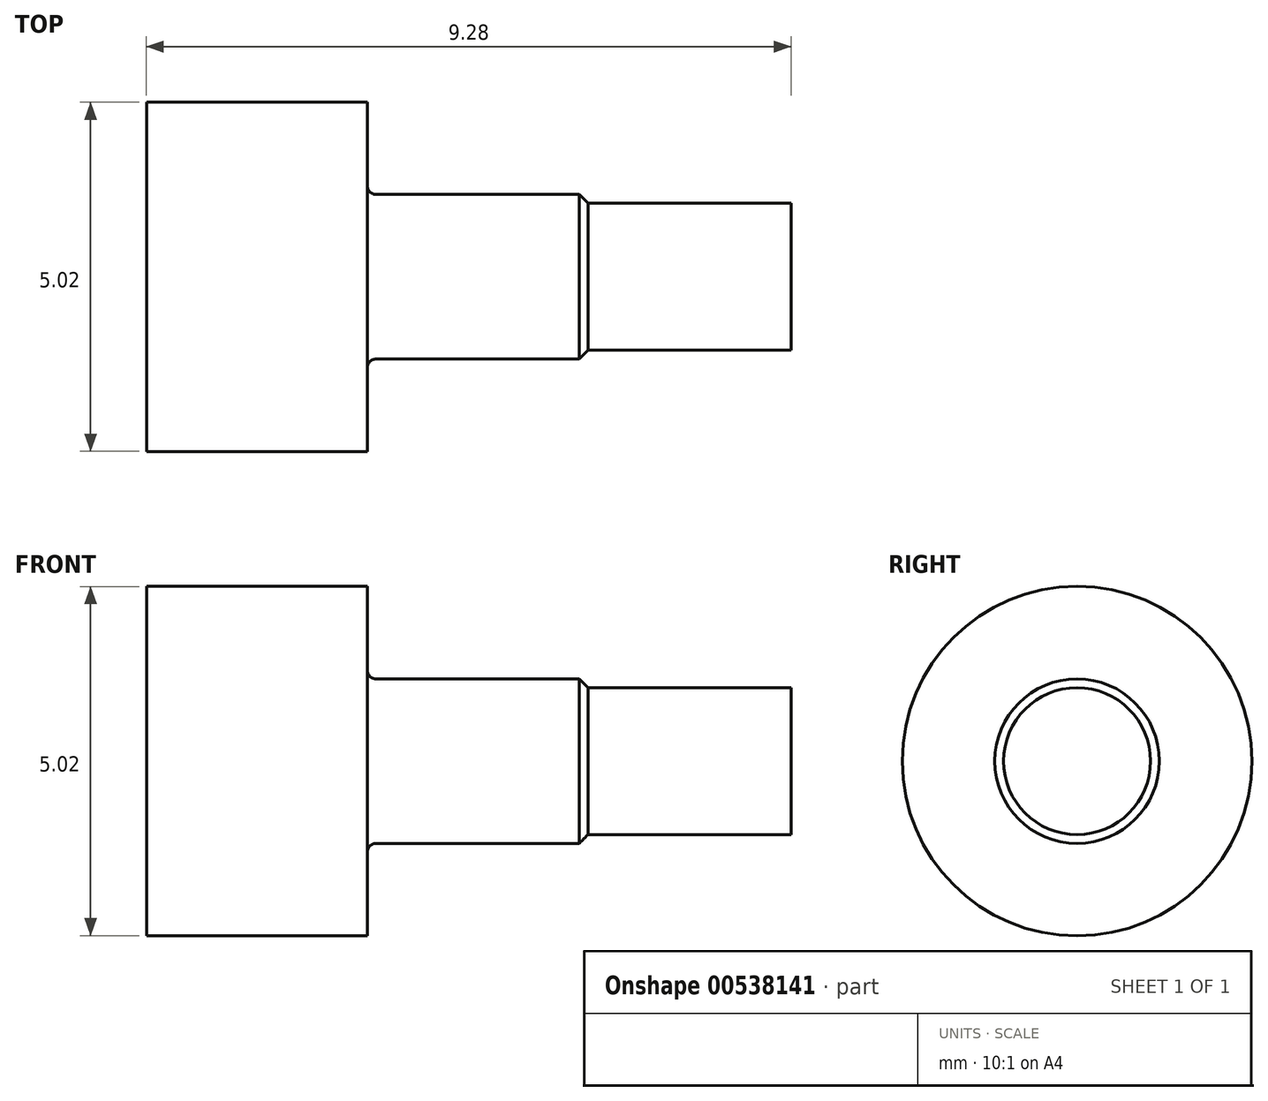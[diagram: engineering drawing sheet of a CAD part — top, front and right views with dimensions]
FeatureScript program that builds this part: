
annotation { "Feature Type Name" : "Feature", "Feature Type Description" : "" }
export const myFeature = defineFeature(function(context is Context, id is Id, definition is map)
    precondition{}
    {
        {
            var Q0;
            Q0=qCreatedBy(makeId("Front.planeOp"),FACE);
            var sketch = newSketch(context, id + "F0", { "sketchPlane" : qUnion([Q0])});
            skLineSegment(sketch, "E0.bottom", {"start": v(0, 0) * mm, "end": v(-3.17, 0) * mm});
            skLineSegment(sketch, "E0.top", {"start": v(0, 2.51) * mm, "end": v(-3.17, 2.51) * mm});
            skLineSegment(sketch, "E0.left", {"start": v(0, 0) * mm, "end": v(0, 2.51) * mm});
            skLineSegment(sketch, "E0.right", {"start": v(-3.18, 0) * mm, "end": v(-3.18, 2.51) * mm});
            skLineSegment(sketch, "E1.bottom", {"start": v(0, 0) * mm, "end": v(3.17, 0) * mm});
            skLineSegment(sketch, "E1.top", {"start": v(0, 1.18) * mm, "end": v(3.18, 1.18) * mm});
            skLineSegment(sketch, "E1.left", {"start": v(0, 0) * mm, "end": v(0, 1.18) * mm});
            skLineSegment(sketch, "E1.right", {"start": v(3.18, 0) * mm, "end": v(3.18, 1.18) * mm});
            skLineSegment(sketch, "E2.bottom", {"start": v(3.18, 0) * mm, "end": v(6.1, 0) * mm});
            skLineSegment(sketch, "E2.top", {"start": v(3.18, 1.06) * mm, "end": v(6.1, 1.06) * mm});
            skLineSegment(sketch, "E2.left", {"start": v(3.18, 0) * mm, "end": v(3.18, 1.06) * mm});
            skLineSegment(sketch, "E2.right", {"start": v(6.1, 0) * mm, "end": v(6.1, 1.06) * mm});
            skSolve(sketch);
        }
        {
            var Q0;
            Q0=makeQuery(id+"F0.imprint","IMPRINT",FACE,{"disambiguationData":[TD([[makeQuery(id+"F0.imprint","IMPRINT",EDGE,{"derivedFrom":sQuery(id+"F0.wireOp",EDGE,"E0.bottom")}),-1.0]])]});
            var Q1;
            Q1=makeQuery(id+"F0.imprint","IMPRINT",FACE,{"disambiguationData":[TD([[makeQuery(id+"F0.imprint","IMPRINT",EDGE,{"derivedFrom":sQuery(id+"F0.wireOp",EDGE,"E1.bottom")}),1.0]])]});
            var Q2;
            Q2=makeQuery(id+"F0.imprint","IMPRINT",FACE,{"disambiguationData":[TD([[makeQuery(id+"F0.imprint","IMPRINT",EDGE,{"derivedFrom":sQuery(id+"F0.wireOp",EDGE,"E2.bottom")}),1.0]])]});
            var Q3;
            Q3=sQuery(id+"F0.wireOp",EDGE,"E0.bottom");
            revolve(context, id + "F1", {"entities" : qUnion([Q0, Q1, Q2]), "axis" : qUnion([Q3]), "revolveType" : RevolveType.ONE_DIRECTION, "angle" : 360 * degree});
        }
        {
            var Q0;
            Q0=makeQuery(id+"F1.opRevolve","SWEPT_EDGE",EDGE,{"disambiguationData":[OSD([sQuery(id+"F0.wireOp",EDGE,"E0.left"),sQuery(id+"F0.wireOp",EDGE,"E1.top"),sQuery(id+"F0.wireOp",EDGE,"E1.left")])]});
            fillet(context, id + "F2", {"entities" : qUnion([Q0]), "radius" : 0.13 * mm, "tangentPropagation" : true, "allowEdgeOverflow" : false});
        }
        {
            var Q0;
            Q0=makeQuery(id+"F1.opRevolve","SWEPT_EDGE",EDGE,{"disambiguationData":[OSD([sQuery(id+"F0.wireOp",EDGE,"E1.top"),sQuery(id+"F0.wireOp",EDGE,"E1.right")])]});
            chamfer(context, id + "F3", {"entities" : qUnion([Q0]), "chamferType" : ChamferType.OFFSET_ANGLE, "width" : 0.13 * mm, "oppositeDirection" : false, "angle" : 45 * degree, "tangentPropagation" : true});
        }
    });
